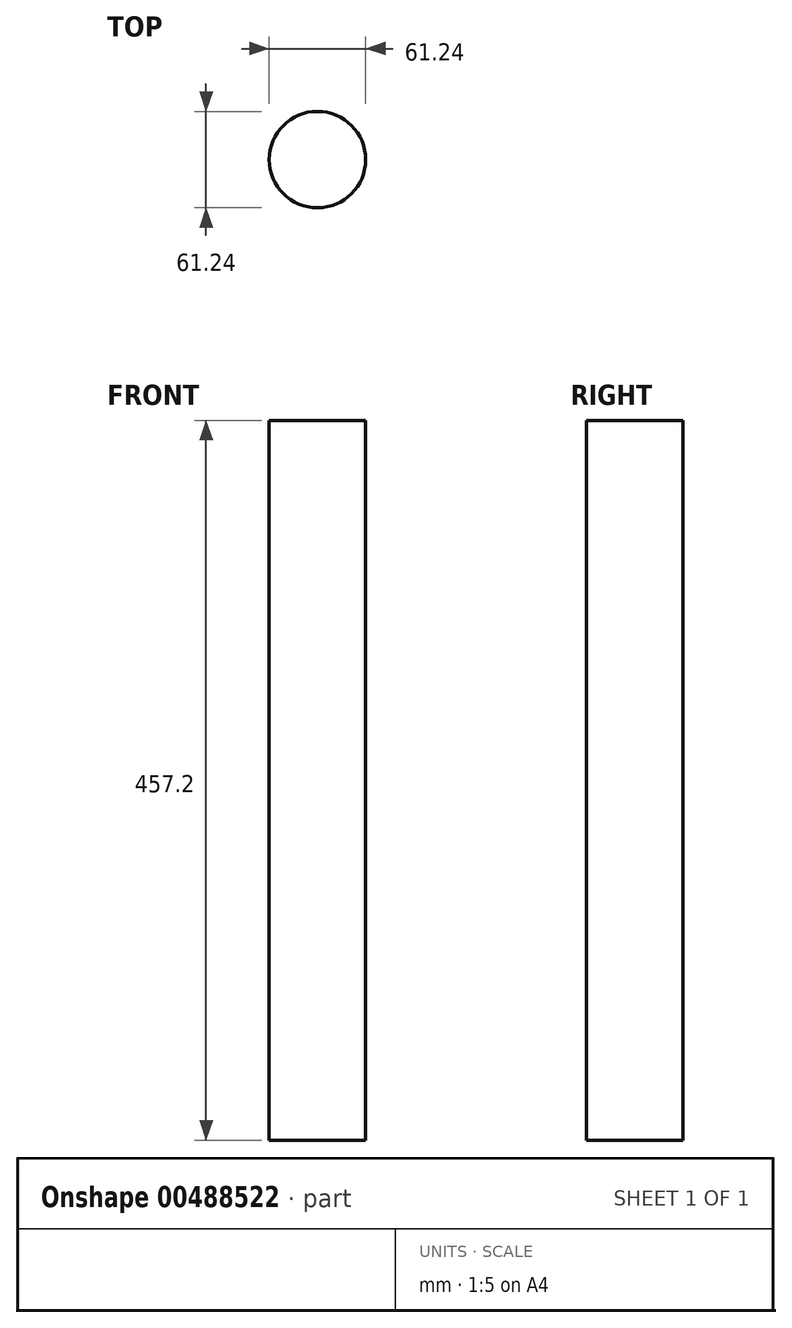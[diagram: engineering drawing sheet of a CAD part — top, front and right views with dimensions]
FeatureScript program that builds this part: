
annotation { "Feature Type Name" : "Feature", "Feature Type Description" : "" }
export const myFeature = defineFeature(function(context is Context, id is Id, definition is map)
    precondition{}
    {
        {
            var Q0;
            Q0=qCreatedBy(makeId("Top.planeOp"),FACE);
            var sketch = newSketch(context, id + "F0", { "sketchPlane" : qUnion([Q0])});
            skCircle(sketch, "E0", {"center": v(0, 0) * mm, "radius": 30.62 * mm});
            skSolve(sketch);
        }
        {
            var Q0;
            Q0=sQuery(id+"F0.wireOp",EDGE,"E0");
            extrude(context, id + "F1", {"bodyType" : ToolBodyType.SURFACE, "surfaceEntities" : qUnion([Q0]), "depth" : 457.2 * mm});
        }
    });
